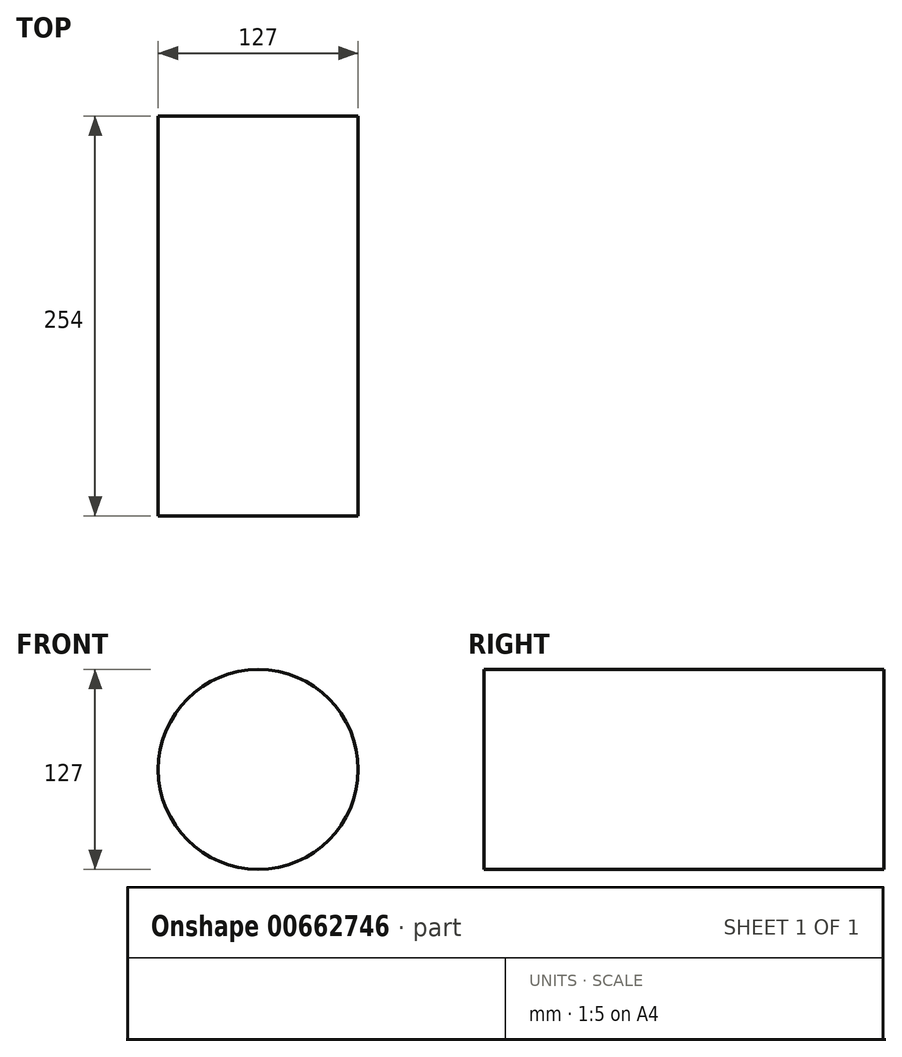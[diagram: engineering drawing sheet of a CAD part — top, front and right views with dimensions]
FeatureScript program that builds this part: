
annotation { "Feature Type Name" : "Feature", "Feature Type Description" : "" }
export const myFeature = defineFeature(function(context is Context, id is Id, definition is map)
    precondition{}
    {
        {
            var Q0;
            Q0=qCreatedBy(makeId("Front.planeOp"),FACE);
            var sketch = newSketch(context, id + "F0", { "sketchPlane" : qUnion([Q0])});
            skCircle(sketch, "E0", {"center": v(0, 0) * mm, "radius": 63.5 * mm});
            skSolve(sketch);
        }
        {
            var Q0;
            Q0=makeQuery(id+"F0.imprint","IMPRINT",FACE,{"disambiguationData":[TD([[makeQuery(id+"F0.imprint","IMPRINT",EDGE,{"derivedFrom":sQuery(id+"F0.wireOp",EDGE,"E0")}),1.0]])]});
            extrude(context, id + "F1", {"entities" : qUnion([Q0]), "endBound" : BoundingType.SYMMETRIC, "depth" : 254 * mm, "offsetDistance" : 25.4 * mm});
        }
    });
